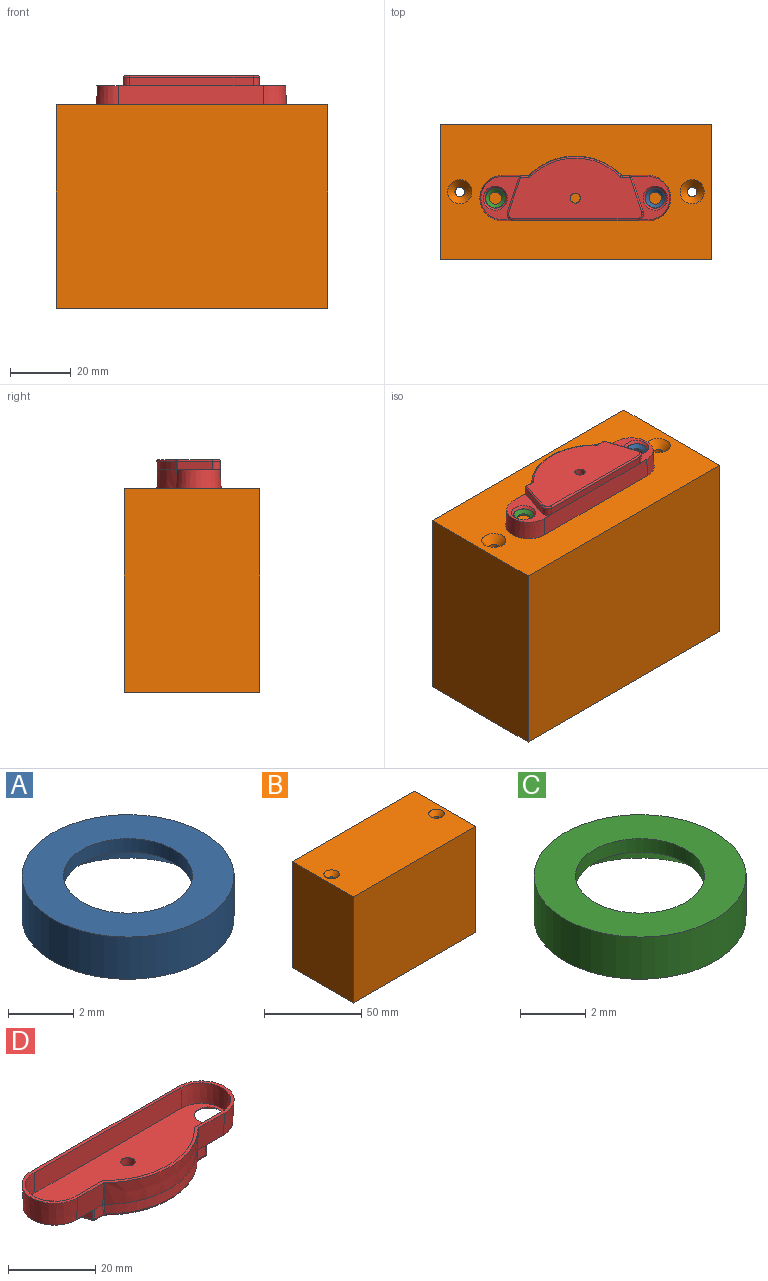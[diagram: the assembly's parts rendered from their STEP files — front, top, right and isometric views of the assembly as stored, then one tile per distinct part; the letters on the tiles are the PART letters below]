
ASSEMBLY  parts=4 mates=3
PART A: 5 faces, bbox 6.5x6.5x1.6 mm
  f0: cylinder r=1.98mm len=3.97mm, axis (0,0,-1), area 6.3mm2, adj f2,f4
  f1: cylinder r=3.26mm len=6.52mm, axis (0,0,-1), area 32.5mm2, adj f2,f3
  f2: plane 6.52x6.52mm, normal (0,0,1), area 21.1mm2, adj f0,f1
  f3: plane 6.52x6.52mm, normal (0,0,-1), area 1.2mm2, adj f1,f4
  f4: cone r=3.2mm half-angle=48.5deg, axis (0,0,-1), area 26.5mm2, adj f0,f3
PART B: 10 faces, bbox 88.9x44.5x66.7 mm
  f0: plane 88.9x66.68mm, normal (0,1,0), area 5927.4mm2, adj f1,f3,f4,f5
  f1: plane 66.68x44.45mm, normal (-1,0,0), area 2963.7mm2, adj f0,f2,f4,f5
  f2: plane 88.9x66.68mm, normal (0,-1,0), area 5927.4mm2, adj f1,f3,f4,f5
  f3: plane 66.68x44.45mm, normal (1,0,0), area 2963.7mm2, adj f0,f2,f4,f5
  f4: plane 88.9x44.45mm, normal (0,0,1), area 3852.3mm2, adj f0,f1,f2,f3,f7,f9
  f5: plane 88.9x44.45mm, normal (0,0,-1), area 3935.8mm2, adj f0,f1,f2,f3,f6,f8
  f6: cylinder r=1.59mm len=63.93mm, axis (0,0,1), area 637.7mm2, adj f5,f7
  f7: cone r=1.59mm half-angle=41deg, axis (0,0,1), area 63.6mm2, adj f4,f6
  f8: cylinder r=1.59mm len=63.93mm, axis (0,0,1), area 637.7mm2, adj f5,f9
  f9: cone r=1.59mm half-angle=41deg, axis (0,0,1), area 63.6mm2, adj f4,f8
PART C: 5 faces, bbox 6.5x6.5x1.6 mm
  f0: cylinder r=1.98mm len=3.97mm, axis (0,0,-1), area 6.3mm2, adj f2,f4
  f1: cylinder r=3.26mm len=6.52mm, axis (0,0,-1), area 32.5mm2, adj f2,f3
  f2: plane 6.52x6.52mm, normal (0,0,1), area 21.1mm2, adj f0,f1
  f3: plane 6.52x6.52mm, normal (0,0,-1), area 1.2mm2, adj f1,f4
  f4: cone r=3.2mm half-angle=48.5deg, axis (0,0,-1), area 26.5mm2, adj f0,f3
PART D: 46 faces, bbox 62.6x22.9x57.9 mm
  f0: plane 14.3x13.08mm, normal (0,0,-1), area 77.8mm2, adj f2,f3,f4,f17,f18,f42,f44
  f1: plane 62.59x21.31mm, normal (0,0,1), area 116.5mm2, adj f2,f3,f4,f5,f6,f7,f9,f10
  f2: plane 47.63x6.35mm, normal (0,1,-0.05), area 302.8mm2, adj f0,f1,f3,f7,f8,f19
  f3: cone r=7.14mm half-angle=3deg, axis (0,0,1), area 146mm2, adj f0,f1,f2,f4
  f4: plane 8.52x6.35mm, normal (0,-1,-0.05), area 53.7mm2, adj f0,f1,f3,f16,f31
  f5: cone r=21.08mm half-angle=3deg, axis (0,0,1), area 211.9mm2, adj f1,f23,f26,f31
  f6: plane 8.52x6.35mm, normal (0,-1,-0.05), area 53.7mm2, adj f1,f7,f8,f22,f26
  f7: cone r=7.14mm half-angle=3deg, axis (0,0,1), area 146mm2, adj f1,f2,f6,f8
  f8: plane 14.3x13.08mm, normal (0,0,-1), area 77.8mm2, adj f2,f6,f7,f20,f21,f25,f43
  f9: plane 47.63x5.54mm, normal (0,-1,0.05), area 264.1mm2, adj f1,f10,f14,f15
  f10: cone r=6.33mm half-angle=3deg, axis (0,0,1), area 113.5mm2, adj f1,f9,f11,f15
  f11: plane 9.06x5.54mm, normal (0,1,0.05), area 49.9mm2, adj f1,f10,f12,f15
  f12: cone r=20.27mm half-angle=3deg, axis (0,0,1), area 183.7mm2, adj f1,f11,f13,f15
  f13: plane 9.06x5.54mm, normal (0,1,0.05), area 49.9mm2, adj f1,f12,f14,f15
  f14: cone r=6.33mm half-angle=3deg, axis (0,0,1), area 113.5mm2, adj f1,f9,f13,f15
  f15: plane 60.37x19.1mm, normal (0,0,1), area 788.5mm2, adj f9,f10,f11,f12,f13,f14,f43,f44
  f16: plane 2.7x2.64mm, normal (0,-1,0.05), area 6.9mm2, adj f4,f34,f39,f42
  f17: plane 11.47x3.91mm, normal (-0.95,-0.32,0.05), area 31.7mm2, adj f0,f18,f40,f42
  f18: cone r=1.98mm half-angle=3deg, axis (0,0,-1), area 10.3mm2, adj f0,f17,f19,f38
  f19: plane 40.54x2.64mm, normal (0,1,0.05), area 107.2mm2, adj f2,f18,f20,f36
  f20: cone r=1.98mm half-angle=3deg, axis (0,0,-1), area 10.3mm2, adj f8,f19,f21,f33
  f21: plane 11.47x3.91mm, normal (0.95,-0.32,0.05), area 31.7mm2, adj f8,f20,f25,f30
  f22: plane 2.7x2.64mm, normal (0,-1,0.05), area 6.9mm2, adj f6,f25,f28,f29
  f23: cone r=21.08mm half-angle=3deg, axis (0,0,-1), area 87.9mm2, adj f5,f28,f34,f35
  f24: plane 43.76x19.9mm, normal (0,0,-1), area 668.7mm2, adj f29,f30,f32,f33,f35,f36,f37,f38
  f25: cylinder r=0.51mm len=2.65mm, axis (-0.04,0.05,1), area 1.7mm2, adj f8,f21,f22,f27
  f26: bspline ~34.2x1.93mm, area 2.5mm2, adj f1,f5,f6,f28
  f27: sphere r=0.51mm, area 0.5mm2, adj f25,f29,f30
  f28: bspline ~49.18x2.72mm, area 1.1mm2, adj f22,f23,f26,f32
  f29: cylinder r=0.51mm len=2.64mm, axis (1,0,0), area 2.2mm2, adj f22,f24,f27,f32
  f30: cylinder r=0.51mm len=11.59mm, axis (0.32,0.95,0), area 9.9mm2, adj f21,f24,f27,f33
  f31: bspline ~34.2x1.93mm, area 2.5mm2, adj f1,f4,f5,f34
  f32: bspline ~0.83x0.72mm, area 0.4mm2, adj f24,f28,f29,f35
  f33: torus R=1.61mm, axis (0,0,-1), area 3mm2, adj f20,f24,f30,f36
  f34: bspline ~49.18x2.72mm, area 1.1mm2, adj f16,f23,f31,f37
  f35: torus R=20.72mm, axis (0,0,-1), area 27.2mm2, adj f23,f24,f32,f37
  f36: cylinder r=0.51mm len=40.54mm, axis (1,0,0), area 33.4mm2, adj f19,f24,f33,f38
  f37: bspline ~0.86x0.69mm, area 0.4mm2, adj f24,f34,f35,f39
  f38: torus R=1.61mm, axis (0,0,-1), area 3mm2, adj f18,f24,f36,f40
  f39: cylinder r=0.51mm len=2.64mm, axis (1,0,0), area 2.2mm2, adj f16,f24,f37,f41
  f40: cylinder r=0.51mm len=11.59mm, axis (-0.32,0.95,0), area 9.9mm2, adj f17,f24,f38,f41
  f41: sphere r=0.51mm, area 0.3mm2, adj f39,f40,f42
  f42: cylinder r=0.51mm len=2.65mm, axis (0.04,0.05,1), area 1.7mm2, adj f0,f16,f17,f41
  f43: cone r=1.27mm half-angle=41deg, axis (0,0,-1), area 24.5mm2, adj f8,f15
  f44: cone r=1.27mm half-angle=41deg, axis (0,0,-1), area 24.5mm2, adj f0,f15
  f45: cylinder r=1.65mm len=3.99mm, axis (0,0,-1), area 41.4mm2, adj f15,f24
PLACE A rot(axis=(1,0,0),180deg) t=(-2.6,10.77,59.82)mm
PLACE B t=(-2.37,12.85,-13.2)mm
PLACE C rot(axis=(1,0,0),180deg) t=(-2.6,10.77,59.82)mm
PLACE D rot(axis=(1,0,0),180deg) t=(-2.6,10.77,59.82)mm fixed
MATE parallel D.f1 <-> B.f4  axis (0,0,-1) through (-2.6,11.92,53.47)mm
MATE cylindrical A.f1 <-> D.f43  axis (0,0,1) through (23.59,10.77,59.01)mm
MATE cylindrical C.f1 <-> D.f44  axis (0,0,1) through (-28.8,10.77,59.01)mm
